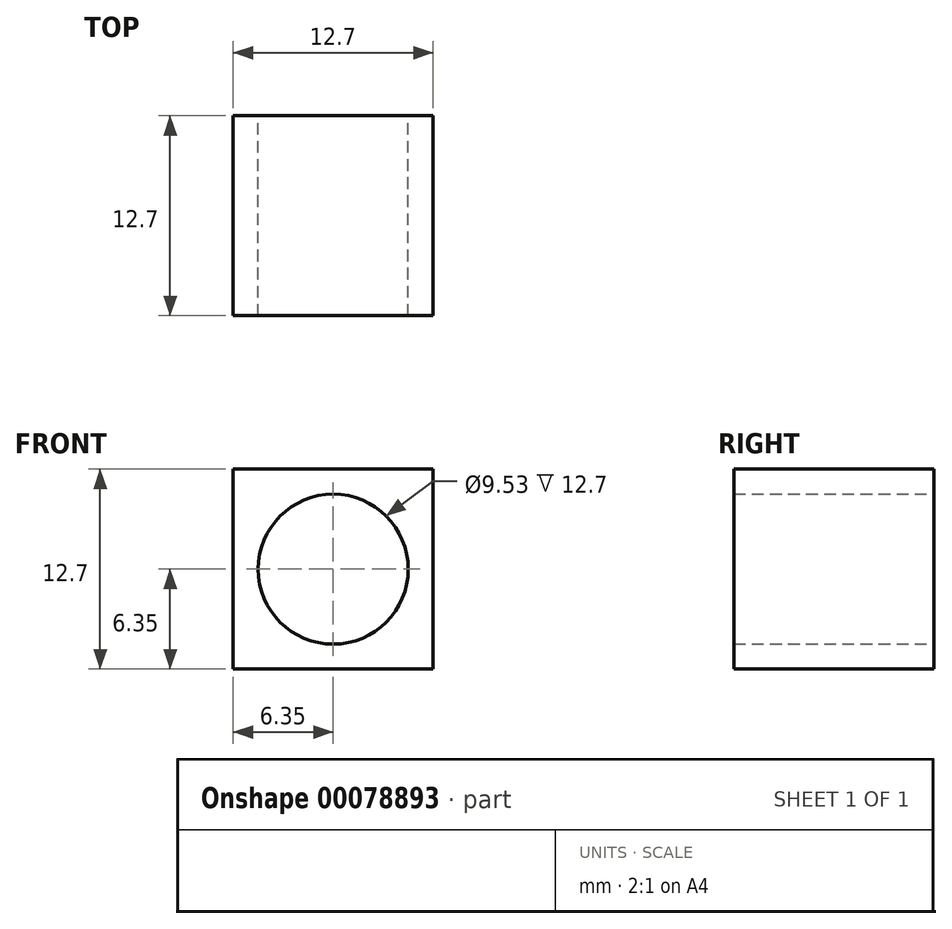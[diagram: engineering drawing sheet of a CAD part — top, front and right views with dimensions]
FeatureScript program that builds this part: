
annotation { "Feature Type Name" : "Feature", "Feature Type Description" : "" }
export const myFeature = defineFeature(function(context is Context, id is Id, definition is map)
    precondition{}
    {
        {
            var Q0;
            Q0=qCreatedBy(makeId("Front.planeOp"),FACE);
            var sketch = newSketch(context, id + "F0", { "sketchPlane" : qUnion([Q0])});
            skLineSegment(sketch, "E0.bottom", {"start": v(6.35, 6.35) * mm, "end": v(-6.35, 6.35) * mm});
            skLineSegment(sketch, "E0.top", {"start": v(6.35, -6.35) * mm, "end": v(-6.35, -6.35) * mm});
            skLineSegment(sketch, "E0.left", {"start": v(6.35, 6.35) * mm, "end": v(6.35, -6.35) * mm});
            skLineSegment(sketch, "E0.right", {"start": v(-6.35, 6.35) * mm, "end": v(-6.35, -6.35) * mm});
            skPoint(sketch, "E0.middle", {"position": v(0, 0) * mm});
            skCircle(sketch, "E1", {"center": v(0, 0) * mm, "radius": 4.76 * mm});
            skSolve(sketch);
        }
        {
            var Q0;
            Q0 = qSketchRegion(id + "F0", true);
            extrude(context, id + "F1", {"entities" : qUnion([Q0]), "depth" : 12.7 * mm});
        }
    });
